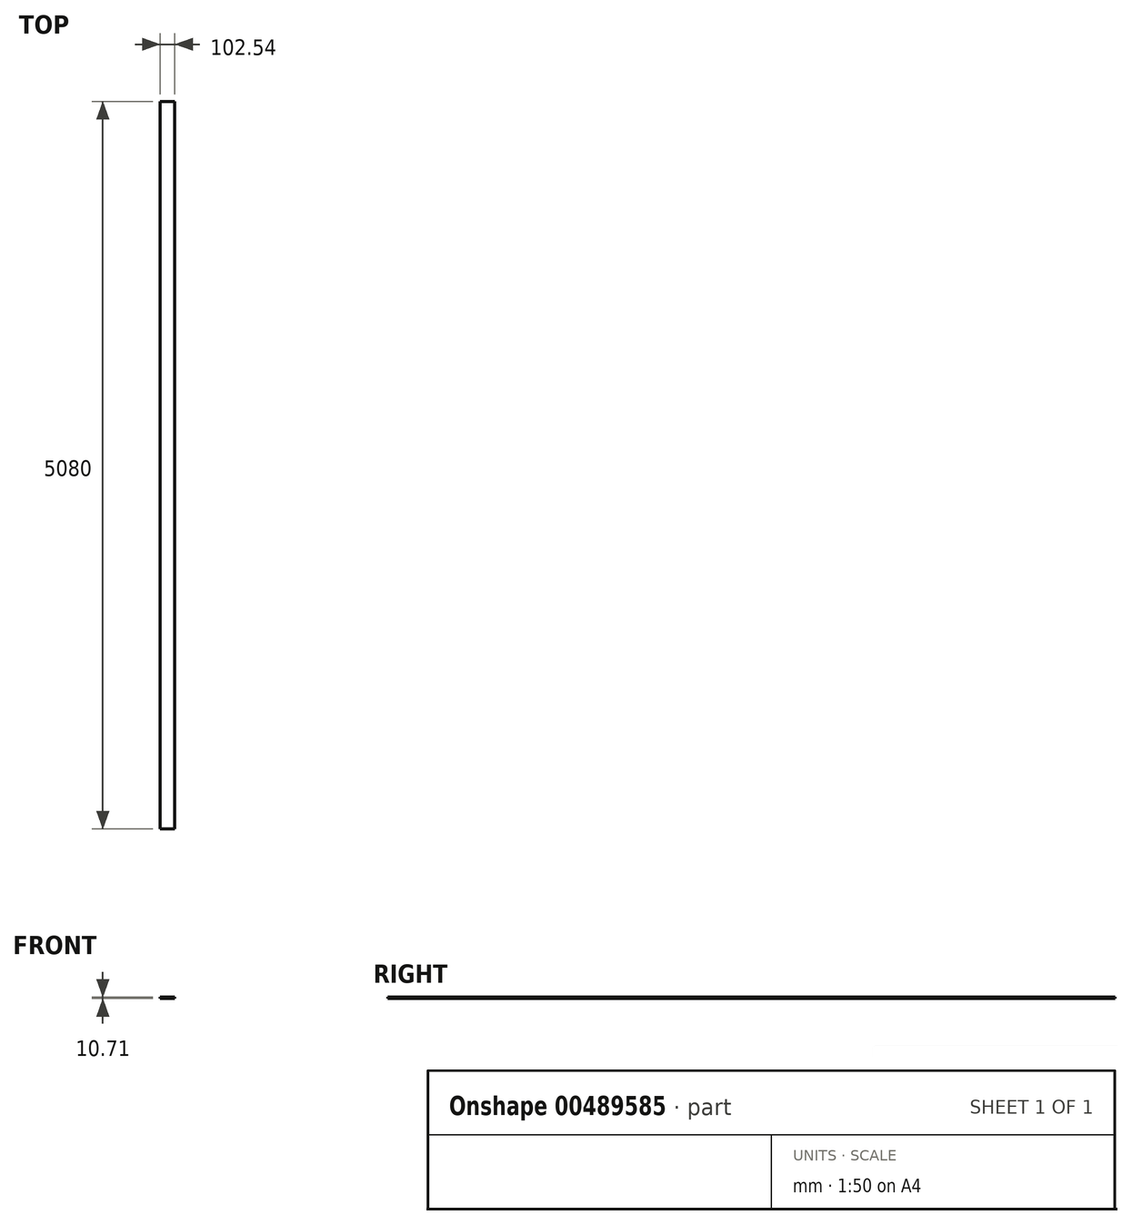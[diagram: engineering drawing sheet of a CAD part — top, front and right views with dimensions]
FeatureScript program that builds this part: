
annotation { "Feature Type Name" : "Feature", "Feature Type Description" : "" }
export const myFeature = defineFeature(function(context is Context, id is Id, definition is map)
    precondition{}
    {
        {
            var Q0;
            Q0=qCreatedBy(makeId("Front.planeOp"),FACE);
            var sketch = newSketch(context, id + "F0", { "sketchPlane" : qUnion([Q0])});
            skLineSegment(sketch, "E0.bottom", {"start": v(-51.27, -8.08) * mm, "end": v(51.27, -8.08) * mm});
            skLineSegment(sketch, "E0.top", {"start": v(-51.27, 2.63) * mm, "end": v(51.27, 2.63) * mm});
            skLineSegment(sketch, "E0.left", {"start": v(-51.27, -8.08) * mm, "end": v(-51.27, 2.63) * mm});
            skLineSegment(sketch, "E0.right", {"start": v(51.27, -8.08) * mm, "end": v(51.27, 2.63) * mm});
            skPoint(sketch, "E0.middle", {"position": v(0, -2.72) * mm});
            skSolve(sketch);
        }
        {
            var Q0;
            Q0=makeQuery(id+"F0.imprint","IMPRINT",FACE,{"disambiguationData":[TD([[makeQuery(id+"F0.imprint","IMPRINT",EDGE,{"derivedFrom":sQuery(id+"F0.wireOp",EDGE,"E0.bottom")}),1.0]])]});
            extrude(context, id + "F1", {"entities" : qUnion([Q0]), "depth" : 5080 * mm});
        }
    });
